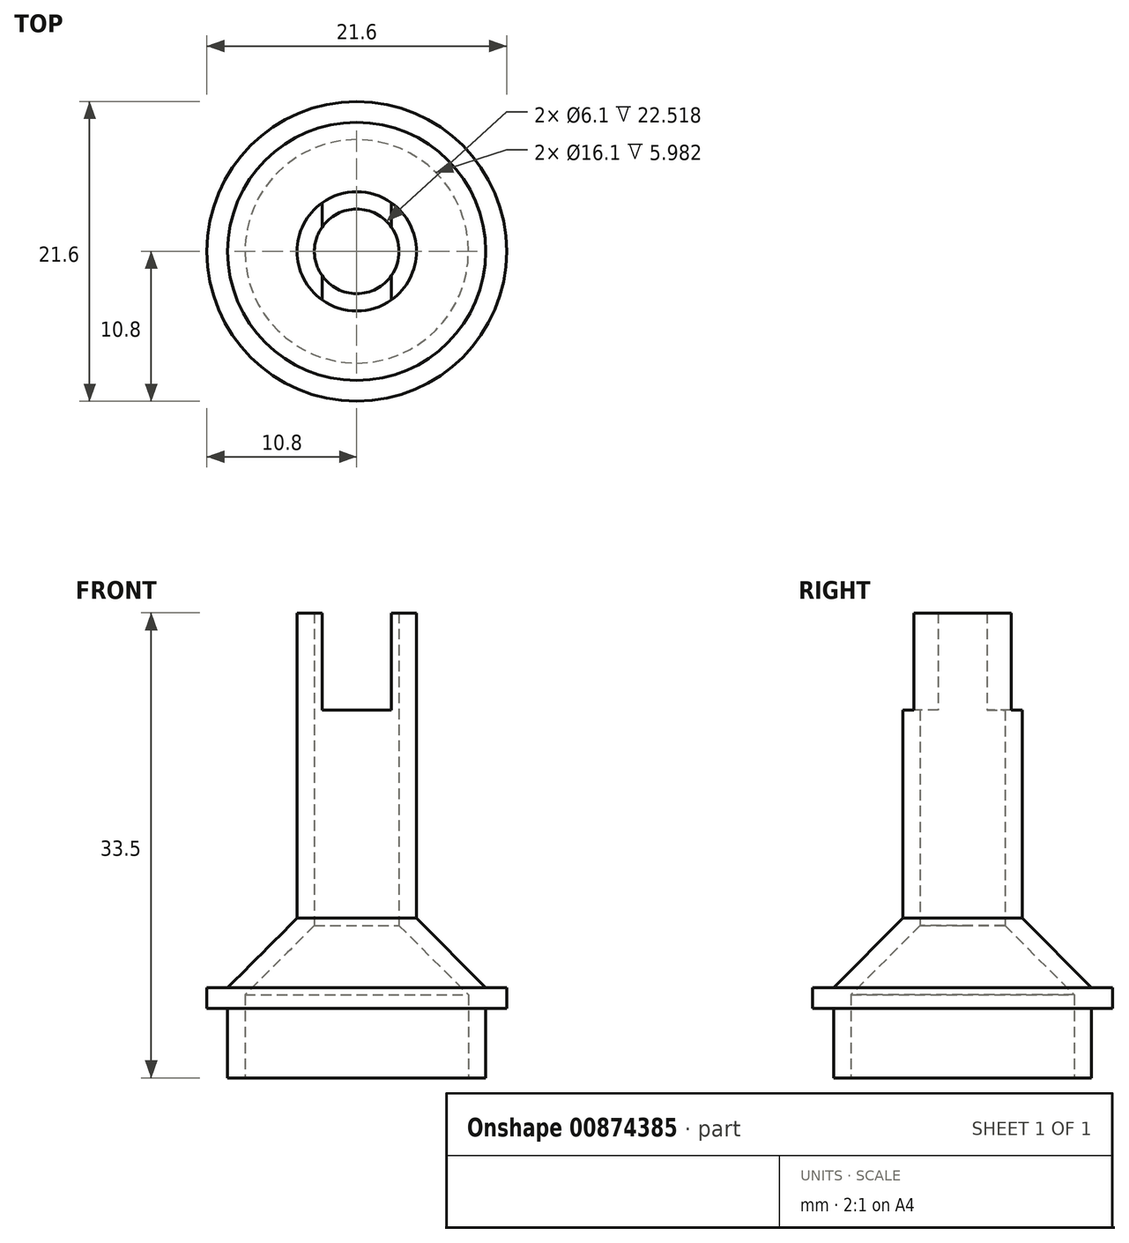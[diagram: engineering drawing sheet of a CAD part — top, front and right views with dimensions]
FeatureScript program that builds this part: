
annotation { "Feature Type Name" : "Feature", "Feature Type Description" : "" }
export const myFeature = defineFeature(function(context is Context, id is Id, definition is map)
    precondition{}
    {
        {
            var Q0;
            Q0=qCreatedBy(makeId("Front.planeOp"),FACE);
            var sketch = newSketch(context, id + "F0", { "sketchPlane" : qUnion([Q0])});
            skLineSegment(sketch, "E0", {"start": v(3.05, 22.52) * mm, "end": v(3.05, 0) * mm});
            skLineSegment(sketch, "E1", {"start": v(3.05, 0) * mm, "end": v(8.05, -5) * mm});
            skLineSegment(sketch, "E2", {"start": v(8.05, -5) * mm, "end": v(8.05, -10.98) * mm});
            skLineSegment(sketch, "E3", {"start": v(8.05, -10.98) * mm, "end": v(9.3, -10.98) * mm});
            skLineSegment(sketch, "E4", {"start": v(9.3, -10.98) * mm, "end": v(9.3, -5.98) * mm});
            skLineSegment(sketch, "E5", {"start": v(9.3, -4.48) * mm, "end": v(4.3, 0.52) * mm});
            skLineSegment(sketch, "E6", {"start": v(4.3, 0.52) * mm, "end": v(4.3, 22.52) * mm});
            skLineSegment(sketch, "E7", {"start": v(4.3, 22.52) * mm, "end": v(3.05, 22.52) * mm});
            skLineSegment(sketch, "E8", {"start": v(9.3, -4.48) * mm, "end": v(10.8, -4.48) * mm});
            skLineSegment(sketch, "E9", {"start": v(10.8, -4.48) * mm, "end": v(10.8, -5.98) * mm});
            skLineSegment(sketch, "E10", {"start": v(10.8, -5.98) * mm, "end": v(9.3, -5.98) * mm});
            skLineSegment(sketch, "E11", {"start": v(0, 0) * mm, "end": v(0, 22.52) * mm, "construction": true});
            skSolve(sketch);
        }
        {
            var Q0;
            Q0 = qSketchRegion(id + "F0", true);
            var Q1;
            Q1=sQuery(id+"F0.wireOp",EDGE,"E11");
            revolve(context, id + "F1", {"surfaceOperationType" : NewSurfaceOperationType.NEW, "entities" : qUnion([Q0]), "axis" : qUnion([Q1]), "revolveType" : RevolveType.FULL});
        }
        {
            var Q0;
            Q0=makeQuery(id+"F1.opRevolve","SWEPT_FACE",FACE,{"disambiguationData":[OSD([sQuery(id+"F0.wireOp",EDGE,"E7")])]});
            var sketch = newSketch(context, id + "F2", { "sketchPlane" : qUnion([Q0])});
            skLineSegment(sketch, "E12.bottom", {"start": v(-2.5, 4.3) * mm, "end": v(2.5, 4.3) * mm});
            skLineSegment(sketch, "E12.top", {"start": v(-2.5, -4.3) * mm, "end": v(2.5, -4.3) * mm});
            skLineSegment(sketch, "E12.left", {"start": v(-2.5, 4.3) * mm, "end": v(-2.5, -4.3) * mm});
            skLineSegment(sketch, "E12.right", {"start": v(2.5, 4.3) * mm, "end": v(2.5, -4.3) * mm});
            skPoint(sketch, "E12.middle", {"position": v(0, 0) * mm});
            skSolve(sketch);
        }
        {
            var Q0;
            Q0 = qSketchRegion(id + "F2", true);
            extrude(context, id + "F3", {"entities" : qUnion([Q0]), "operationType" : NewBodyOperationType.REMOVE, "oppositeDirection" : true, "depth" : 7 * mm, "offsetDistance" : 25 * mm});
        }
    });
